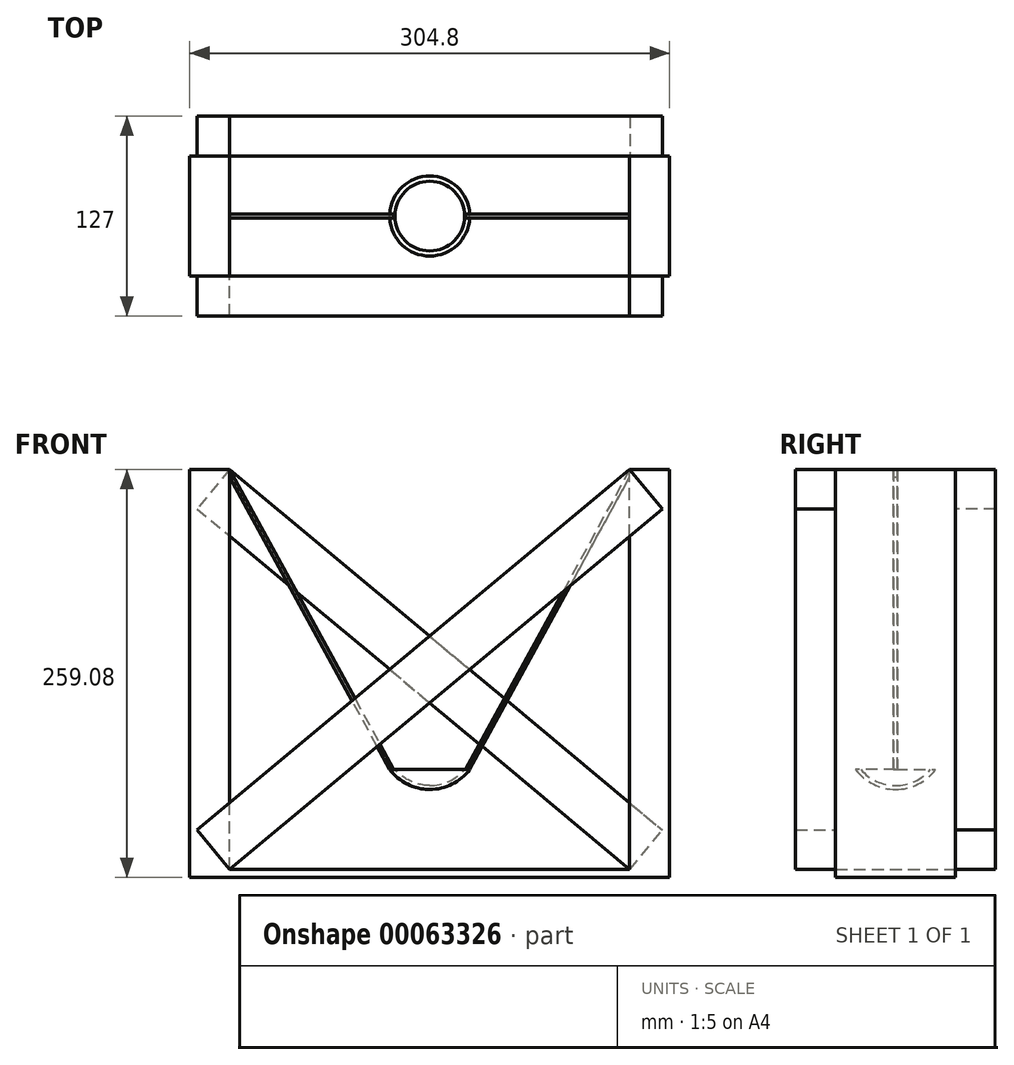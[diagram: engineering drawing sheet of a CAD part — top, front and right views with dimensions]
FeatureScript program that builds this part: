
annotation { "Feature Type Name" : "Feature", "Feature Type Description" : "" }
export const myFeature = defineFeature(function(context is Context, id is Id, definition is map)
    precondition{}
    {
        {
            var Q0;
            Q0=qCreatedBy(makeId("Front.planeOp"),FACE);
            var sketch = newSketch(context, id + "F0", { "sketchPlane" : qUnion([Q0])});
            skLineSegment(sketch, "E0", {"start": v(0, 0) * mm, "end": v(25.4, 0) * mm});
            skLineSegment(sketch, "E1", {"start": v(0, 0) * mm, "end": v(0, -12.7) * mm});
            skLineSegment(sketch, "E2", {"start": v(0, -12.7) * mm, "end": v(6.24, -12.7) * mm, "construction": true});
            skArc(sketch, "E3", {"start": v(0, -12.7) * mm, "mid": v(14.2, -9.35) * mm, "end": v(25.4, 0) * mm});
            skSolve(sketch);
        }
        {
            var Q0;
            Q0 = qSketchRegion(id + "F0", true);
            var Q1;
            Q1=sQuery(id+"F0.wireOp",EDGE,"E1");
            revolve(context, id + "F1", {"entities" : qUnion([Q0]), "axis" : qUnion([Q1]), "revolveType" : RevolveType.FULL});
        }
        {
            var Q0;
            Q0=makeQuery(id+"F1.opRevolve","SWEPT_FACE",FACE,{"disambiguationData":[OSD([sQuery(id+"F0.wireOp",EDGE,"E0")])]});
            shell(context, id + "F2", {"entities" : qUnion([Q0]), "thickness" : 2.54 * mm});
        }
        {
            var Q0;
            Q0=qCreatedBy(makeId("Front.planeOp"),FACE);
            var sketch = newSketch(context, id + "F3", { "sketchPlane" : qUnion([Q0])});
            skLineSegment(sketch, "E4", {"start": v(0, 0) * mm, "end": v(0, -63.5) * mm, "construction": true});
            skLineSegment(sketch, "E5", {"start": v(0, -63.5) * mm, "end": v(127, -63.5) * mm, "construction": true});
            skLineSegment(sketch, "E6.bottom", {"start": v(127, -63.5) * mm, "end": v(152.4, -63.5) * mm});
            skLineSegment(sketch, "E6.top", {"start": v(127, 190.5) * mm, "end": v(152.4, 190.5) * mm});
            skLineSegment(sketch, "E6.left", {"start": v(127, -63.5) * mm, "end": v(127, 190.5) * mm});
            skLineSegment(sketch, "E6.right", {"start": v(152.4, -63.5) * mm, "end": v(152.4, 190.5) * mm});
            skSolve(sketch);
        }
        {
            var Q0;
            Q0 = qSketchRegion(id + "F3", true);
            extrude(context, id + "F4", {"entities" : qUnion([Q0]), "endBound" : BoundingType.SYMMETRIC, "depth" : 76.2 * mm});
        }
        {
            var Q0;
            Q0=makeQuery(id+"F4.opExtrude","SWEPT_BODY",BODY,{"disambiguationData":[OSD([sQuery(id+"F3.wireOp",EDGE,"E6.bottom"),sQuery(id+"F3.wireOp",EDGE,"E6.top"),sQuery(id+"F3.wireOp",EDGE,"E6.left"),sQuery(id+"F3.wireOp",EDGE,"E6.right")])]});
            var Q1;
            Q1=qCreatedBy(makeId("Right.planeOp"),FACE);
            mirror(context, id + "F5", {"entities" : qUnion([Q0]), "mirrorPlane" : qUnion([Q1])});
        }
        {
            var Q0;
            Q0=makeQuery(id+"F4.opExtrude","CAP_FACE",FACE,{"disambiguationData":[OSD([sQuery(id+"F3.wireOp",EDGE,"E6.bottom"),sQuery(id+"F3.wireOp",EDGE,"E6.top"),sQuery(id+"F3.wireOp",EDGE,"E6.left"),sQuery(id+"F3.wireOp",EDGE,"E6.right")])],"isStart":false});
            var sketch = newSketch(context, id + "F6", { "sketchPlane" : qUnion([Q0])});
            skLineSegment(sketch, "E7", {"start": v(152.4, -63.5) * mm, "end": v(-152.4, -63.5) * mm, "construction": true});
            skLineSegment(sketch, "E8", {"start": v(152.4, 190.5) * mm, "end": v(-152.4, 190.5) * mm, "construction": true});
            skLineSegment(sketch, "E9", {"start": v(-152.4, 190.5) * mm, "end": v(-152.4, -63.5) * mm, "construction": true});
            skLineSegment(sketch, "E10", {"start": v(152.4, 190.5) * mm, "end": v(152.4, -63.5) * mm, "construction": true});
            skLineSegment(sketch, "E11", {"start": v(-152.4, -63.5) * mm, "end": v(152.4, 190.5) * mm, "construction": true});
            skLineSegment(sketch, "E12", {"start": v(152.4, -63.5) * mm, "end": v(-152.4, 190.5) * mm, "construction": true});
            skLineSegment(sketch, "E13", {"start": v(127, 190.5) * mm, "end": v(-147.83, -38.52) * mm});
            skLineSegment(sketch, "E14", {"start": v(147.82, 165.52) * mm, "end": v(-127.01, -63.5) * mm});
            skLineSegment(sketch, "E15", {"start": v(-127.01, -63.5) * mm, "end": v(-147.83, -38.52) * mm});
            skLineSegment(sketch, "E16", {"start": v(127, 190.5) * mm, "end": v(147.82, 165.52) * mm});
            skPoint(sketch, "E17.orphan", {"position": v(152.4, 169.34) * mm});
            skSolve(sketch);
        }
        {
            var Q0;
            Q0 = qSketchRegion(id + "F6", true);
            extrude(context, id + "F7", {"entities" : qUnion([Q0]), "depth" : 25.4 * mm});
        }
        {
            var Q0;
            Q0=makeQuery(id+"F7.opExtrude","SWEPT_BODY",BODY,{"disambiguationData":[OSD([sQuery(id+"F6.wireOp",EDGE,"E13"),sQuery(id+"F6.wireOp",EDGE,"E14"),sQuery(id+"F6.wireOp",EDGE,"E15"),sQuery(id+"F6.wireOp",EDGE,"E16")])]});
            var Q1;
            Q1=qCreatedBy(makeId("Front.planeOp"),FACE);
            mirror(context, id + "F8", {"entities" : qUnion([Q0]), "mirrorPlane" : qUnion([Q1])});
        }
        {
            var Q0;
            Q0=makeQuery(id+"F8.opPattern","COPY",BODY,{"derivedFrom":makeQuery(id+"F7.opExtrude","SWEPT_BODY",BODY,{"disambiguationData":[OSD([sQuery(id+"F6.wireOp",EDGE,"E13"),sQuery(id+"F6.wireOp",EDGE,"E14"),sQuery(id+"F6.wireOp",EDGE,"E15"),sQuery(id+"F6.wireOp",EDGE,"E16")])]}),"instanceName":"1"});
            var Q1;
            Q1=qCreatedBy(makeId("Right.planeOp"),FACE);
            mirror(context, id + "F9", {"entities" : qUnion([Q0]), "mirrorPlane" : qUnion([Q1])});
        }
        {
            var Q0;
            Q0=makeQuery(id+"F8.opPattern","COPY",BODY,{"derivedFrom":makeQuery(id+"F7.opExtrude","SWEPT_BODY",BODY,{"disambiguationData":[OSD([sQuery(id+"F6.wireOp",EDGE,"E13"),sQuery(id+"F6.wireOp",EDGE,"E14"),sQuery(id+"F6.wireOp",EDGE,"E15"),sQuery(id+"F6.wireOp",EDGE,"E16")])]}),"instanceName":"1"});
            deleteBodies(context, id + "F10", {"entities" : qUnion([Q0])});
        }
        {
            var Q0;
            Q0=qCreatedBy(makeId("Front.planeOp"),FACE);
            var sketch = newSketch(context, id + "F11", { "sketchPlane" : qUnion([Q0])});
            skLineSegment(sketch, "E18", {"start": v(0, 0) * mm, "end": v(-22.86, 0) * mm, "construction": true});
            skLineSegment(sketch, "E19", {"start": v(0, 0) * mm, "end": v(0, 190.5) * mm, "construction": true});
            skLineSegment(sketch, "E20", {"start": v(0, 190.5) * mm, "end": v(-127, 190.5) * mm, "construction": true});
            skLineSegment(sketch, "E21", {"start": v(-127, 190.5) * mm, "end": v(-22.86, 0) * mm});
            skLineSegment(sketch, "E22", {"start": v(-22.86, 0) * mm, "end": v(-25.4, 0) * mm, "construction": true});
            skLineSegment(sketch, "E23", {"start": v(-127, 190.5) * mm, "end": v(-127, 115.1) * mm, "construction": true});
            skLineSegment(sketch, "E24", {"start": v(-25.4, 0) * mm, "end": v(-127, 185.85) * mm});
            skLineSegment(sketch, "E25", {"start": v(-127, 185.85) * mm, "end": v(-127, 190.5) * mm});
            skLineSegment(sketch, "E26", {"start": v(-22.86, 0) * mm, "end": v(-25.4, 0) * mm});
            skSolve(sketch);
        }
        {
            var Q0;
            Q0 = qSketchRegion(id + "F11", true);
            extrude(context, id + "F12", {"entities" : qUnion([Q0]), "endBound" : BoundingType.SYMMETRIC, "depth" : 2.54 * mm});
        }
        {
            var Q0;
            Q0=makeQuery(id+"F12.opExtrude","SWEPT_BODY",BODY,{"disambiguationData":[OSD([sQuery(id+"F11.wireOp",EDGE,"E21"),sQuery(id+"F11.wireOp",EDGE,"E24"),sQuery(id+"F11.wireOp",EDGE,"E25"),sQuery(id+"F11.wireOp",EDGE,"E26")])]});
            var Q1;
            Q1=qCreatedBy(makeId("Right.planeOp"),FACE);
            mirror(context, id + "F13", {"entities" : qUnion([Q0]), "mirrorPlane" : qUnion([Q1])});
        }
        {
            var Q0;
            Q0=makeQuery(id+"F5.opPattern","COPY",FACE,{"derivedFrom":makeQuery(id+"F4.opExtrude","SWEPT_FACE",FACE,{"disambiguationData":[OSD([sQuery(id+"F3.wireOp",EDGE,"E6.bottom")])]}),"instanceName":"1"});
            var sketch = newSketch(context, id + "F14", { "sketchPlane" : qUnion([Q0])});
            skLineSegment(sketch, "E27.rect.bottom", {"start": v(-152.4, 38.1) * mm, "end": v(152.4, 38.1) * mm});
            skLineSegment(sketch, "E27.rect.top", {"start": v(-152.4, -38.1) * mm, "end": v(152.4, -38.1) * mm});
            skLineSegment(sketch, "E27.rect.left", {"start": v(-152.4, 38.1) * mm, "end": v(-152.4, -38.1) * mm});
            skLineSegment(sketch, "E27.rect.right", {"start": v(152.4, 38.1) * mm, "end": v(152.4, -38.1) * mm});
            skPoint(sketch, "E27.rect.middle", {"position": v(0, 0) * mm});
            skSolve(sketch);
        }
        {
            var Q0;
            Q0 = qSketchRegion(id + "F14", true);
            extrude(context, id + "F15", {"entities" : qUnion([Q0]), "operationType" : NewBodyOperationType.ADD, "depth" : 5.08 * mm});
        }
    });
